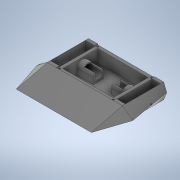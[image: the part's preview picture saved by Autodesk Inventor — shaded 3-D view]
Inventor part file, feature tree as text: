
AUTODESK INVENTOR PART (.ipt)
format: ipt  version: 2020 (Build 240168000, 168)  size: 430,080 bytes
history: native  units: in
note: dims shown in document units (in); Inventor stores cm internally (conversion verified against a paired STEP export)
features: sketch x19, extrude x17, projected_geometry x14, mirror x4, plane x2, loft x1
ambient origin geometry x8: Origin, YZ Plane, XZ Plane, XY Plane, X Axis, Y Axis, Z Axis, Center Point
bodies: Solid1 (feature_tree)
feature tree (57):
  extrude  "Extrusion1"  Depth=4.3307in
  extrude  "Extrusion2"  TaperAngle=0.0deg  [1 undecoded]
  extrude  "Extrusion3"  Depth=0.2362in
  extrude  "Extrusion4"  Depth=0.6299in
  extrude  "Extrusion13"  Depth=0.0787in
  mirror  "Mirror7"
  extrude  "Extrusion14"  Depth=0.6102in
  extrude  "Extrusion15"  Depth=0.4724in
  extrude  "Extrusion16"  Depth=0.1575in
  mirror  "Mirror8"
  extrude  "Extrusion17"  TaperAngle=0.0deg  [1 undecoded]
  extrude  "Extrusion18"  Depth=1.1811in
  extrude  "Extrusion25"  TaperAngle=0.0deg  [1 undecoded]
  sketch  "Sketch31"  dims[d46=0.1181in d47=0.0in d48=0.7874in d49=0.0in]
  sketch  "Sketch32"  dims[d50=0.2362in d51=0.7874in d52=0.0in]
  extrude  "Extrusion26"  Depth=0.7874in TaperAngle=0.0deg
  extrude  "Extrusion27"  Depth=0.2362in TaperAngle=0.0deg
  plane  "Work Plane9"
  sketch  "Sketch33"  dims[d74=0.0625in d75=0.0625in]
  plane  "Work Plane10"
  sketch  "Sketch34"  dims[d76=0.7in d77=0.0in]
  extrude  "Extrusion28"  Depth=0.0625in
  extrude  "Extrusion29"  TaperAngle=0.0deg  [1 undecoded]
  loft  "Loft2"
  extrude  "Extrusion30"  TaperAngle=0.0deg  [1 undecoded]
  mirror  "Mirror11"
  extrude  "Extrusion31"  TaperAngle=0.0deg  [1 undecoded]
  mirror  "Mirror12"
  sketch  "Sketch1"  dims[d0=4.3307in d1=2.3622in]
  sketch  "Sketch2"  dims[d2=0.1181in d3=0.0in]
  projected_geometry  "Projected Loop1"
  sketch  "Sketch3"  dims[d4=0.2362in d5=1.0005in]
  projected_geometry  "Projected Loop2"
  sketch  "Sketch4"  dims[d6=0.0in d7=0.6299in]
  projected_geometry  "Projected Loop3"
  sketch  "Sketch13"  dims[d8=0.5906in d9=0.0787in]
  sketch  "Sketch14"  dims[d11=0.4429in d12=0.0in d13=0.6102in]
  projected_geometry  "Projected Loop8"
  sketch  "Sketch15"  dims[d14=0.6102in d15=0.4724in]
  projected_geometry  "Projected Loop9"
  sketch  "Sketch16"  dims[d16=0.7874in d17=0.0in d38=0.1575in]
  projected_geometry  "Projected Loop10"
  sketch  "Sketch17"  dims[d39=2.3622in d40=0.0in]
  projected_geometry  "Projected Loop11"
  sketch  "Sketch19"  dims[d41=0.7in d42=0.0in d43=1.1811in]
  projected_geometry  "Projected Loop13"
  sketch  "Sketch29"  dims[d44=0.2362in d45=0.0in]
  projected_geometry  "Projected Loop19"
  projected_geometry  "Projected Loop20"
  projected_geometry  "Projected Loop21"
  sketch  "Sketch35"  dims[d78=2.3622in d79=0.7874in]
  projected_geometry  "Projected Loop22"
  sketch  "Sketch36"  dims[d80=0.7in d81=0.0in]
  sketch  "Sketch37"  dims[d82=0.7in d83=0.0in]
  projected_geometry  "Projected Loop23"
  sketch  "Sketch38"  dims[d84=0.5008in d85=0.0in d86=0.4334in d87=0.0in d88=0.2362in d89=0.0in d90=90.0deg d91=0.0in d92=90.0deg d93=1.1812in d94=0.0in d95=0.1181in d96=0.1102in d97=0.1102in d98=0.2362in d99=0.0in d68=0.0197in d69=0.0344in d70=0.0197in d71=0.0344in]
  projected_geometry  "Projected Loop24"
note: 6 required parameter values undecoded (feature->parameter linkage not recoverable at this tier; creation-order binding heuristic only, values carry confidence <= 0.55)
